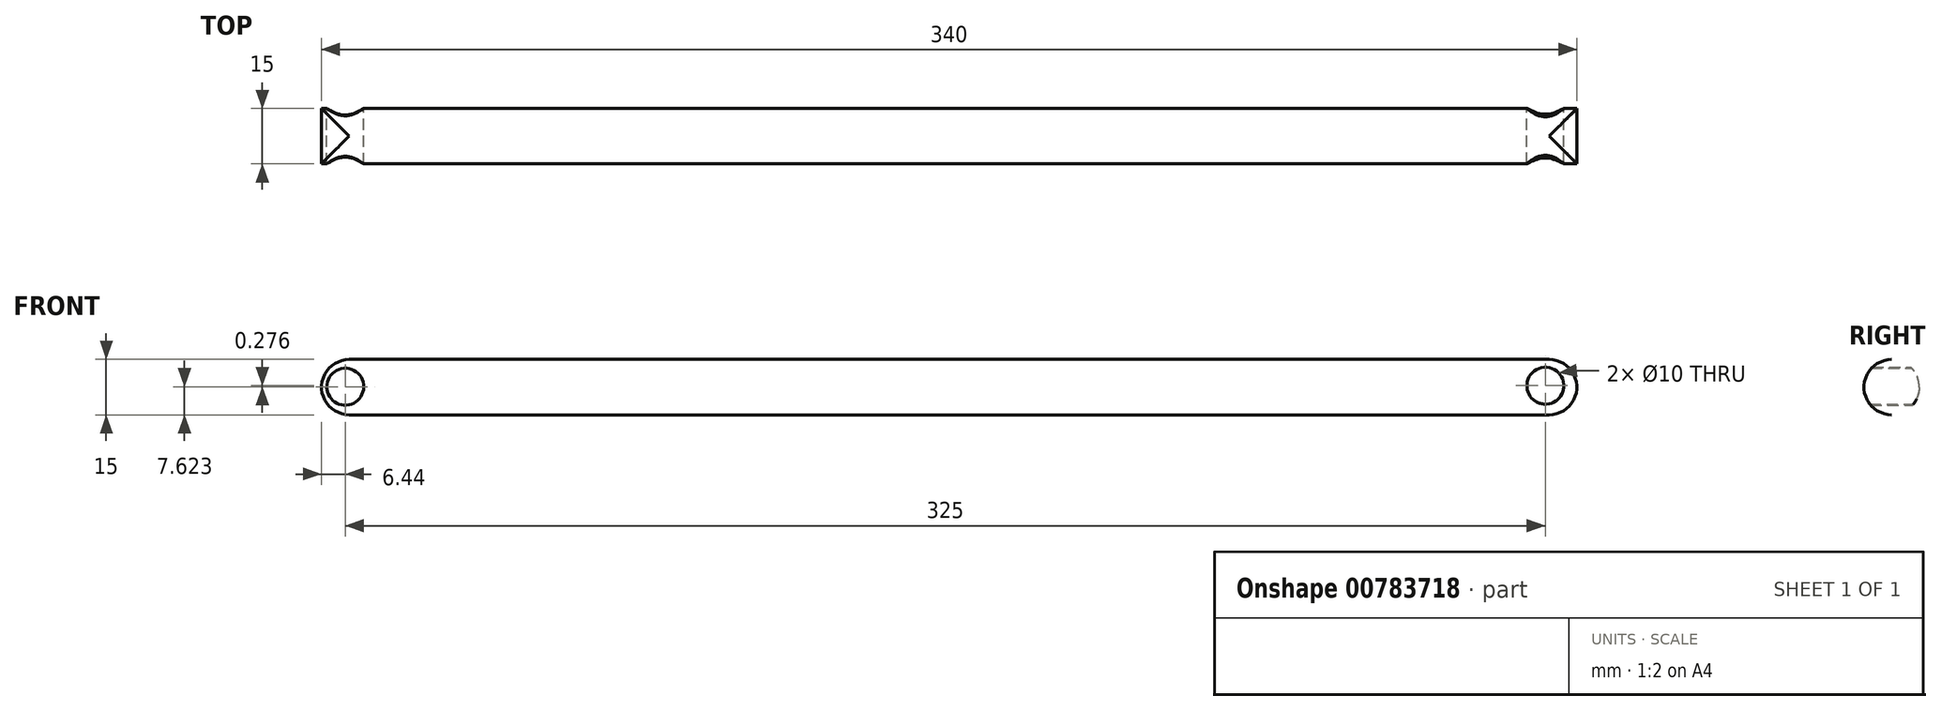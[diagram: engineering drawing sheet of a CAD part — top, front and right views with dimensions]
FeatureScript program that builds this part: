
annotation { "Feature Type Name" : "Feature", "Feature Type Description" : "" }
export const myFeature = defineFeature(function(context is Context, id is Id, definition is map)
    precondition{}
    {
        {
            var Q0;
            Q0=qCreatedBy(makeId("Front.planeOp"),FACE);
            var sketch = newSketch(context, id + "F0", { "sketchPlane" : qUnion([Q0])});
            skLineSegment(sketch, "E0.bottom", {"start": v(-340, 15) * mm, "end": v(0, 15) * mm});
            skLineSegment(sketch, "E0.top", {"start": v(-340, 0) * mm, "end": v(0, 0) * mm});
            skLineSegment(sketch, "E0.left", {"start": v(-340, 15) * mm, "end": v(-340, 0) * mm});
            skLineSegment(sketch, "E0.right", {"start": v(0, 15) * mm, "end": v(0, 0) * mm});
            skSolve(sketch);
        }
        {
            var Q0;
            Q0=makeQuery(id+"F0.imprint","IMPRINT",FACE,{"disambiguationData":[TD([[makeQuery(id+"F0.imprint","IMPRINT",EDGE,{"derivedFrom":sQuery(id+"F0.wireOp",EDGE,"E0.bottom")}),-1.0]])]});
            extrude(context, id + "F1", {"entities" : qUnion([Q0]), "depth" : 15 * mm, "offsetDistance" : 25 * mm});
        }
        {
            var Q0;
            Q0=qCreatedBy(makeId("Front.planeOp"),FACE);
            var sketch = newSketch(context, id + "F2", { "sketchPlane" : qUnion([Q0])});
            skCircle(sketch, "E1", {"center": v(-333.56, 7.62) * mm, "radius": 5 * mm});
            skCircle(sketch, "E2", {"center": v(-8.56, 7.9) * mm, "radius": 5 * mm});
            skSolve(sketch);
        }
        {
            var Q0;
            Q0=qSketchRegion(id+"F2",true);
            extrude(context, id + "F3", {"entities" : qUnion([Q0]), "operationType" : NewBodyOperationType.REMOVE, "depth" : 20 * mm, "offsetDistance" : 25 * mm});
        }
        {
            var Q0;
            Q0=makeQuery(id+"F1.opExtrude","CAP_EDGE",EDGE,{"disambiguationData":[OSD([sQuery(id+"F0.wireOp",EDGE,"E0.bottom")])],"isStart":true});
            var Q1;
            Q1=makeQuery(id+"F1.opExtrude","CAP_EDGE",EDGE,{"disambiguationData":[OSD([sQuery(id+"F0.wireOp",EDGE,"E0.top")])],"isStart":true});
            var Q2;
            Q2=makeQuery(id+"F1.opExtrude","CAP_EDGE",EDGE,{"disambiguationData":[OSD([sQuery(id+"F0.wireOp",EDGE,"E0.bottom")])],"isStart":false});
            var Q3;
            Q3=makeQuery(id+"F1.opExtrude","CAP_EDGE",EDGE,{"disambiguationData":[OSD([sQuery(id+"F0.wireOp",EDGE,"E0.top")])],"isStart":false});
            var Q4;
            Q4=makeQuery(id+"F1.opExtrude","SWEPT_EDGE",EDGE,{"disambiguationData":[OSD([sQuery(id+"F0.wireOp",EDGE,"E0.bottom"),sQuery(id+"F0.wireOp",EDGE,"E0.right")])]});
            var Q5;
            Q5=makeQuery(id+"F1.opExtrude","SWEPT_EDGE",EDGE,{"disambiguationData":[OSD([sQuery(id+"F0.wireOp",EDGE,"E0.top"),sQuery(id+"F0.wireOp",EDGE,"E0.right")])]});
            var Q6;
            Q6=makeQuery(id+"F1.opExtrude","SWEPT_EDGE",EDGE,{"disambiguationData":[OSD([sQuery(id+"F0.wireOp",EDGE,"E0.bottom"),sQuery(id+"F0.wireOp",EDGE,"E0.left")])]});
            var Q7;
            Q7=makeQuery(id+"F1.opExtrude","SWEPT_EDGE",EDGE,{"disambiguationData":[OSD([sQuery(id+"F0.wireOp",EDGE,"E0.top"),sQuery(id+"F0.wireOp",EDGE,"E0.left")])]});
            fillet(context, id + "F4", {"entities" : qUnion([Q0, Q1, Q2, Q3, Q4, Q5, Q6, Q7]), "radius" : 7.5 * mm, "tangentPropagation" : true, "allowEdgeOverflow" : false});
        }
    });
